# Revit family: Shower-Handshower-KOHLER-Rainduet-K-24717IN-1
name_source: partatom
category: Plumbing Fixtures
units: mm (PartAtom-declared; Revit-internal decimal feet)

## family parameters
Cut with Voids When Loaded = No
Host = Face
OmniClass Number = 23.31.17.00
OmniClass Title = Showers
Part Type = Normal
Room Calculation Point = No
Round Connector Dimension = Use Diameter
Shared = No

## types (6) — shared parameters
ADA Compliant = No
Assembly Code = D2010700
CW Connection = No
Cold Water Inlet = Cold Water Inlet
Date Modified = 08/20/2024
Default Elevation = 42"
Description = Handshower Without Hose
Drain Included = No
Flow Rate = 0 GPM
HW Connection = Yes
Height = 9 11/16"
Hot Water Inlet = Hot Water Inlet
Length = 2 11/16"
Manufacturer = Kohler Co.
Master Format 2014 = 22 42 23
Master Format 2014 Name = Residential Showers
Material = Plastic
Pressure = 0.00 psi
Product Name = Rainduet
Tempered Water Inlet = Tempered Water Inlet
URL = https://www.kohler.co.in
Vent Connection = No
Waste Connection = No
Waste Water Outlet = Waste Water Outlet
WaterSense Certified = No
Width = 4 15/16"

## per-type parameters (varying)
| type | Finish | Model | Product Page URL | Secondary Finish | Type |
| BL-Matte Black | Kohler-Plastic-BL-Matte_Black | K-24717IN-BL |  | Plastic-Pantone-PQ-194205-TCX | 2 |
| AF-Vibrant French Gold | KOHLER-Plastic-AF-Vibrant_French_Gold | K-24717IN-AF | https://www.kohler.co.in | Kohler-Plastic-0-White | 1 |
| BV-Brushed Bronze | Kohler-Plastic-BV-Brushed_Bronze | K-24717IN-BV | https://www.kohler.co.in | Kohler-Plastic-0-White | 3 |
| RGD-Polished Rose Gold | Kohler-Plastic-RGD-Polished_Rose_Gold | K-24717IN-RGD | https://www.kohler.co.in | Kohler-Plastic-0-White | 5 |
| CP-Polished Chrome | Kohler-Plastic-CP-Polished_Chrome | K-24717IN-CP | https://www.kohler.co.in | Kohler-Plastic-0-White | 4 |
| BRD-Brushed Rose Gold | KOHLER-Metal-BRD-Brushed_Rose_Gold | K-24717IN-BRD |  | Kohler-Plastic-0-White | 6 |

## geometry (parser evidence)
native form markers: Sweep x4
no freeform markers — native parametric forms only
